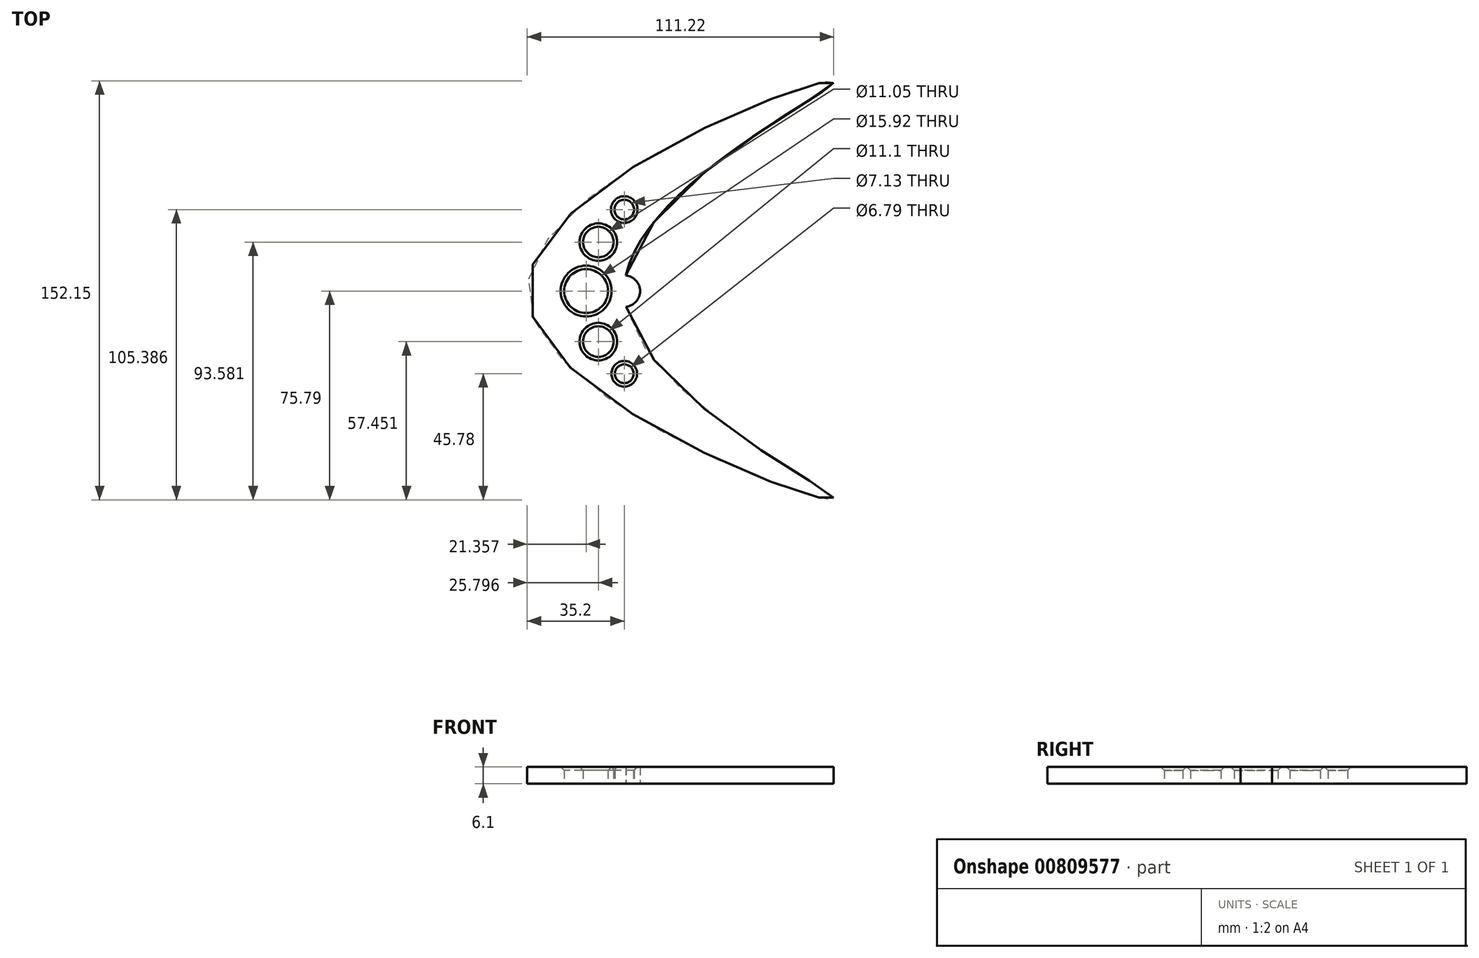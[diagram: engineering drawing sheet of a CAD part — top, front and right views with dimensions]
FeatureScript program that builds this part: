
annotation { "Feature Type Name" : "Feature", "Feature Type Description" : "" }
export const myFeature = defineFeature(function(context is Context, id is Id, definition is map)
    precondition{}
    {
        {
            var Q0;
            Q0=qCreatedBy(makeId("Top.planeOp"),FACE);
            var sketch = newSketch(context, id + "F0", { "sketchPlane" : qUnion([Q0])});
            skFitSpline(sketch, "E0", {"points": [v(0, 0) * mm, v(75.91, 76.2) * mm, v(-35.2, 0) * mm, v(75.91, -75.63) * mm, v(0, 0) * mm]});
            skCircle(sketch, "E1", {"center": v(0, 0) * mm, "radius": 5.73 * mm});
            skSolve(sketch);
        }
        {
            var Q0;
            {var subQ0=sQuery(id+"F0.wireOp",EDGE,"E1");var subQ1=sQuery(id+"F0.wireOp",EDGE,"E0");var subQ2=makeQuery(id+"F0.imprint","INTERSECT",VERTEX,{"disambiguationData":[OD(0.0)],"derivedFrom":[subQ1,subQ0]});Q0=makeQuery(id+"F0.imprint","IMPRINT",FACE,{"disambiguationData":[TD([[makeQuery(id+"F0.imprint","IMPRINT",EDGE,{"disambiguationData":[TD([[subQ2,1.0]])],"derivedFrom":subQ1}),1.0]])]});}
            var Q1;
            {var subQ0=sQuery(id+"F0.wireOp",EDGE,"E1");var subQ1=sQuery(id+"F0.wireOp",EDGE,"E0");var subQ2=makeQuery(id+"F0.imprint","INTERSECT",VERTEX,{"disambiguationData":[OD(0.0)],"derivedFrom":[subQ1,subQ0]});Q1=makeQuery(id+"F0.imprint","IMPRINT",FACE,{"disambiguationData":[TD([[makeQuery(id+"F0.imprint","IMPRINT",EDGE,{"disambiguationData":[TD([[subQ2,-1.0]])],"derivedFrom":subQ1}),-1.0]])]});}
            var Q2;
            {var subQ0=sQuery(id+"F0.wireOp",EDGE,"E1");var subQ1=sQuery(id+"F0.wireOp",EDGE,"E0");var subQ2=makeQuery(id+"F0.imprint","INTERSECT",VERTEX,{"disambiguationData":[OD(0.0)],"derivedFrom":[subQ1,subQ0]});Q2=makeQuery(id+"F0.imprint","IMPRINT",FACE,{"disambiguationData":[TD([[makeQuery(id+"F0.imprint","IMPRINT",EDGE,{"disambiguationData":[TD([[subQ2,-1.0]])],"derivedFrom":subQ1}),1.0]])]});}
            extrude(context, id + "F1", {"entities" : qUnion([Q0, Q1, Q2]), "depth" : 6.1 * mm, "offsetDistance" : 25.4 * mm});
        }
        {
            var Q0;
            Q0=qCreatedBy(makeId("Top.planeOp"),FACE);
            var sketch = newSketch(context, id + "F2", { "sketchPlane" : qUnion([Q0])});
            skCircle(sketch, "E2", {"center": v(-13.84, 0) * mm, "radius": 7.96 * mm});
            skCircle(sketch, "E3", {"center": v(-9.4, 17.8) * mm, "radius": 5.53 * mm});
            skCircle(sketch, "E4", {"center": v(-9.4, -18.34) * mm, "radius": 5.55 * mm});
            skCircle(sketch, "E5", {"center": v(0, 29.6) * mm, "radius": 3.56 * mm});
            skCircle(sketch, "E6", {"center": v(0, -30.01) * mm, "radius": 3.4 * mm});
            skSolve(sketch);
        }
        {
            var Q0;
            Q0=makeQuery(id+"F2.imprint","IMPRINT",FACE,{"disambiguationData":[TD([[makeQuery(id+"F2.imprint","IMPRINT",EDGE,{"derivedFrom":sQuery(id+"F2.wireOp",EDGE,"E3")}),1.0]])]});
            var Q1;
            Q1=makeQuery(id+"F2.imprint","IMPRINT",FACE,{"disambiguationData":[TD([[makeQuery(id+"F2.imprint","IMPRINT",EDGE,{"derivedFrom":sQuery(id+"F2.wireOp",EDGE,"E2")}),1.0]])]});
            var Q2;
            Q2=makeQuery(id+"F2.imprint","IMPRINT",FACE,{"disambiguationData":[TD([[makeQuery(id+"F2.imprint","IMPRINT",EDGE,{"derivedFrom":sQuery(id+"F2.wireOp",EDGE,"E4")}),1.0]])]});
            var Q3;
            Q3=makeQuery(id+"F2.imprint","IMPRINT",FACE,{"disambiguationData":[TD([[makeQuery(id+"F2.imprint","IMPRINT",EDGE,{"derivedFrom":sQuery(id+"F2.wireOp",EDGE,"E5")}),1.0]])]});
            var Q4;
            Q4=makeQuery(id+"F2.imprint","IMPRINT",FACE,{"disambiguationData":[TD([[makeQuery(id+"F2.imprint","IMPRINT",EDGE,{"derivedFrom":sQuery(id+"F2.wireOp",EDGE,"E6")}),1.0]])]});
            extrude(context, id + "F3", {"entities" : qUnion([Q0, Q1, Q2, Q3, Q4]), "operationType" : NewBodyOperationType.REMOVE, "depth" : 95 * mm, "offsetDistance" : 25.4 * mm});
        }
        {
            var Q0;
            Q0=makeQuery(id+"F3.boolean.opBoolean","INTERSECT",EDGE,{"derivedFrom":[makeQuery(id+"F1.opExtrude","CAP_FACE",FACE,{"disambiguationData":[OSD([sQuery(id+"F0.wireOp",EDGE,"E0"),sQuery(id+"F0.wireOp",EDGE,"E1")])],"isStart":false}),makeQuery(id+"F3.opExtrude","SWEPT_FACE",FACE,{"disambiguationData":[OSD([sQuery(id+"F2.wireOp",EDGE,"E2")])]})]});
            var Q1;
            Q1=makeQuery(id+"F3.boolean.opBoolean","INTERSECT",EDGE,{"derivedFrom":[makeQuery(id+"F1.opExtrude","CAP_FACE",FACE,{"disambiguationData":[OSD([sQuery(id+"F0.wireOp",EDGE,"E0"),sQuery(id+"F0.wireOp",EDGE,"E1")])],"isStart":false}),makeQuery(id+"F3.opExtrude","SWEPT_FACE",FACE,{"disambiguationData":[OSD([sQuery(id+"F2.wireOp",EDGE,"E3")])]})]});
            var Q2;
            Q2=makeQuery(id+"F3.boolean.opBoolean","INTERSECT",EDGE,{"derivedFrom":[makeQuery(id+"F1.opExtrude","CAP_FACE",FACE,{"disambiguationData":[OSD([sQuery(id+"F0.wireOp",EDGE,"E0"),sQuery(id+"F0.wireOp",EDGE,"E1")])],"isStart":false}),makeQuery(id+"F3.opExtrude","SWEPT_FACE",FACE,{"disambiguationData":[OSD([sQuery(id+"F2.wireOp",EDGE,"E5")])]})]});
            var Q3;
            Q3=makeQuery(id+"F3.boolean.opBoolean","INTERSECT",EDGE,{"derivedFrom":[makeQuery(id+"F1.opExtrude","CAP_FACE",FACE,{"disambiguationData":[OSD([sQuery(id+"F0.wireOp",EDGE,"E0"),sQuery(id+"F0.wireOp",EDGE,"E1")])],"isStart":false}),makeQuery(id+"F3.opExtrude","SWEPT_FACE",FACE,{"disambiguationData":[OSD([sQuery(id+"F2.wireOp",EDGE,"E4")])]})]});
            var Q4;
            Q4=makeQuery(id+"F3.boolean.opBoolean","INTERSECT",EDGE,{"derivedFrom":[makeQuery(id+"F1.opExtrude","CAP_FACE",FACE,{"disambiguationData":[OSD([sQuery(id+"F0.wireOp",EDGE,"E0"),sQuery(id+"F0.wireOp",EDGE,"E1")])],"isStart":false}),makeQuery(id+"F3.opExtrude","SWEPT_FACE",FACE,{"disambiguationData":[OSD([sQuery(id+"F2.wireOp",EDGE,"E6")])]})]});
            var Q5;
            Q5=makeQuery(id+"FwChWJ91tf0D2WS_1.opExtrude","CAP_EDGE",EDGE,{"disambiguationData":[OSD([sQuery(id+"FOk7KcD4IchcPJp_1.wireOp",EDGE,"bKSBUzj0-s7kt-Lh1x-z4ls-56QMHEePgXxL")])],"isStart":false});
            var Q6;
            Q6=makeQuery(id+"FwChWJ91tf0D2WS_1.opExtrude","CAP_EDGE",EDGE,{"disambiguationData":[OSD([sQuery(id+"FOk7KcD4IchcPJp_1.wireOp",EDGE,"bKSBUzj0-s7kt-Lh1x-z4ls-56QMHEePgXxL")])],"isStart":true});
            var Q7;
            Q7=makeQuery(id+"F3.boolean.opBoolean","COPY",EDGE,{"derivedFrom":makeQuery(id+"F3.opExtrude","CAP_EDGE",EDGE,{"disambiguationData":[OSD([sQuery(id+"F2.wireOp",EDGE,"E4")])],"isStart":true})});
            var Q8;
            Q8=makeQuery(id+"F3.boolean.opBoolean","COPY",EDGE,{"derivedFrom":makeQuery(id+"F3.opExtrude","CAP_EDGE",EDGE,{"disambiguationData":[OSD([sQuery(id+"F2.wireOp",EDGE,"E2")])],"isStart":true})});
            var Q9;
            Q9=makeQuery(id+"F3.boolean.opBoolean","COPY",EDGE,{"derivedFrom":makeQuery(id+"F3.opExtrude","CAP_EDGE",EDGE,{"disambiguationData":[OSD([sQuery(id+"F2.wireOp",EDGE,"E3")])],"isStart":true})});
            var Q10;
            Q10=makeQuery(id+"F3.boolean.opBoolean","COPY",EDGE,{"derivedFrom":makeQuery(id+"F3.opExtrude","CAP_EDGE",EDGE,{"disambiguationData":[OSD([sQuery(id+"F2.wireOp",EDGE,"E5")])],"isStart":true})});
            var Q11;
            Q11=makeQuery(id+"F3.boolean.opBoolean","COPY",EDGE,{"derivedFrom":makeQuery(id+"F3.opExtrude","CAP_EDGE",EDGE,{"disambiguationData":[OSD([sQuery(id+"F2.wireOp",EDGE,"E6")])],"isStart":true})});
            chamfer(context, id + "F4", {"entities" : qUnion([Q0, Q1, Q2, Q3, Q4, Q5, Q6, Q7, Q8, Q9, Q10, Q11]), "width" : 1.27 * mm, "tangentPropagation" : true});
        }
    });
